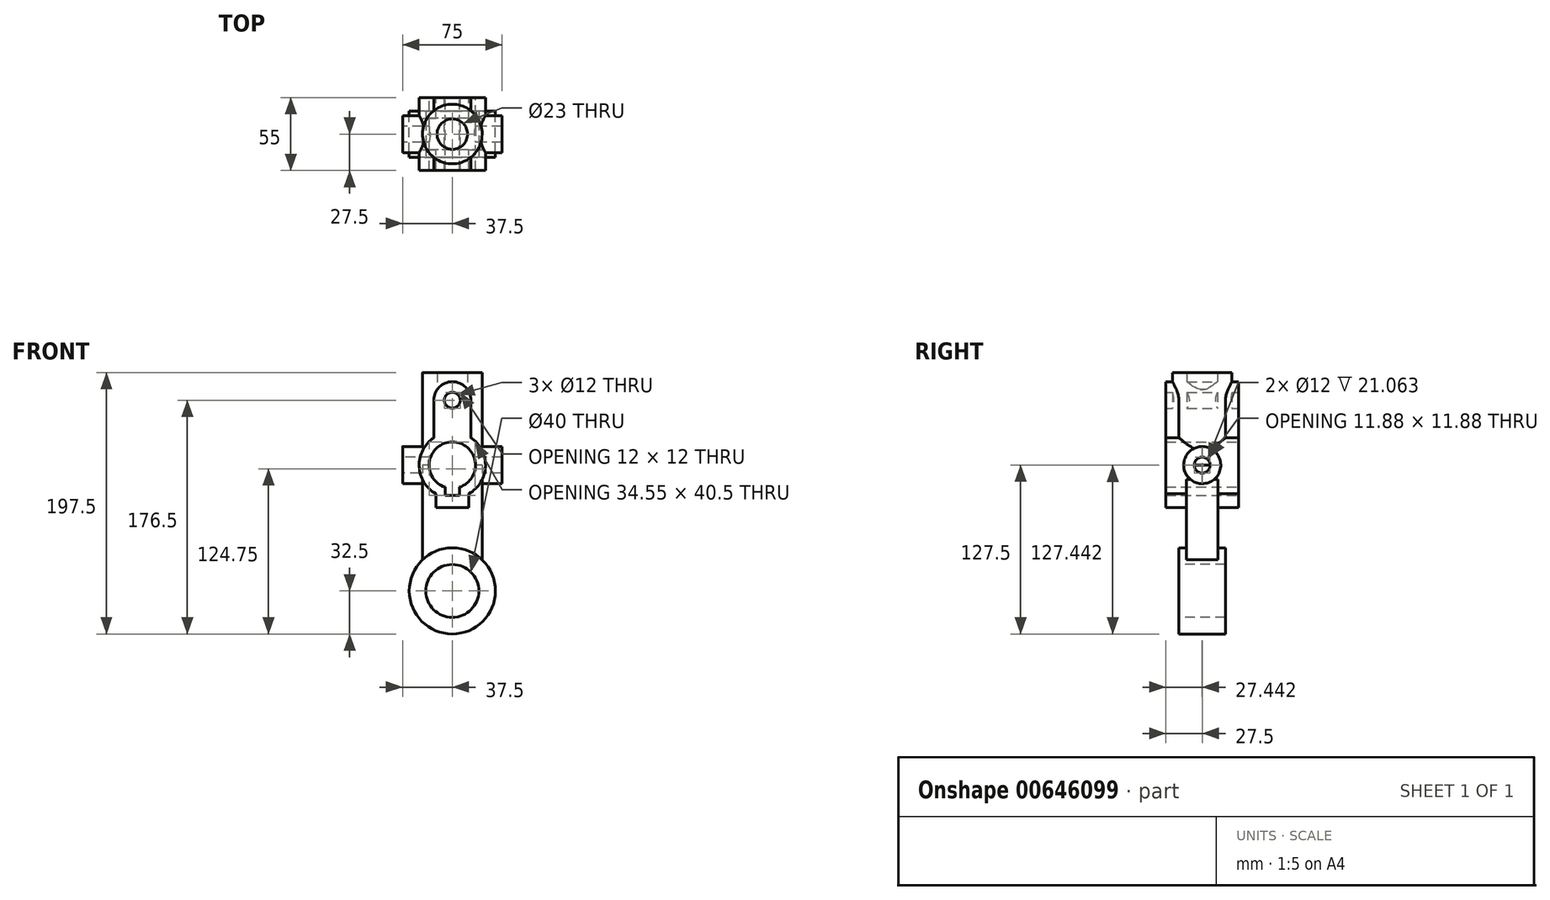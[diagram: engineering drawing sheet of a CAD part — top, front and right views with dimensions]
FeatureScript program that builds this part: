
annotation { "Feature Type Name" : "Feature", "Feature Type Description" : "" }
export const myFeature = defineFeature(function(context is Context, id is Id, definition is map)
    precondition{}
    {
        {
            var Q0;
            Q0=qCreatedBy(makeId("Top.planeOp"),FACE);
            var sketch = newSketch(context, id + "F0", { "sketchPlane" : qUnion([Q0])});
            skCircle(sketch, "E0", {"center": v(0, 0) * mm, "radius": 11.5 * mm});
            skCircle(sketch, "E1", {"center": v(0, 0) * mm, "radius": 22.5 * mm});
            skSolve(sketch);
        }
        {
            var Q0;
            Q0=makeQuery(id+"F0.imprint","IMPRINT",FACE,{"disambiguationData":[TD([[makeQuery(id+"F0.imprint","IMPRINT",EDGE,{"derivedFrom":sQuery(id+"F0.wireOp",EDGE,"E0")}),-1.0]])]});
            extrude(context, id + "F1", {"entities" : qUnion([Q0]), "depth" : 70 * mm, "offsetDistance" : 25 * mm});
        }
        {
            var Q0;
            Q0=qCreatedBy(makeId("Front.planeOp"),FACE);
            var sketch = newSketch(context, id + "F2", { "sketchPlane" : qUnion([Q0])});
            skArc(sketch, "E2", {"start": v(5.5, -16.61) * mm, "mid": v(0, 17.5) * mm, "end": v(-5.5, -16.61) * mm});
            skLineSegment(sketch, "E3", {"start": v(0, -23) * mm, "end": v(-5.5, -23) * mm});
            skLineSegment(sketch, "E4", {"start": v(-5.5, -23) * mm, "end": v(5.5, -23) * mm});
            skLineSegment(sketch, "E5", {"start": v(-5.5, -23) * mm, "end": v(-5.5, -16.61) * mm});
            skLineSegment(sketch, "E6", {"start": v(5.5, -23) * mm, "end": v(5.5, -16.61) * mm});
            skArc(sketch, "E7", {"start": v(12.5, -21.65) * mm, "mid": v(24.98, -0.88) * mm, "end": v(14, 20.71) * mm});
            skLineSegment(sketch, "E8", {"start": v(0, -32) * mm, "end": v(-12.5, -32) * mm});
            skLineSegment(sketch, "E9", {"start": v(0, -32) * mm, "end": v(12.5, -32) * mm});
            skLineSegment(sketch, "E10", {"start": v(12.5, -32) * mm, "end": v(12.5, -21.65) * mm});
            skLineSegment(sketch, "E11", {"start": v(-12.5, -32) * mm, "end": v(-12.5, -21.65) * mm});
            skPoint(sketch, "E12.endSnap0", {"position": v(0, 25) * mm});
            skCircle(sketch, "E13", {"center": v(0, 49) * mm, "radius": 6 * mm});
            skArc(sketch, "E14", {"start": v(14, 49) * mm, "mid": v(0, 63) * mm, "end": v(-14, 49) * mm});
            skLineSegment(sketch, "E15", {"start": v(-14, 49) * mm, "end": v(14, 49) * mm});
            skLineSegment(sketch, "E16", {"start": v(14, 49) * mm, "end": v(-14, 49) * mm});
            skLineSegment(sketch, "E17", {"start": v(-14, 49) * mm, "end": v(-14, 20.71) * mm});
            skLineSegment(sketch, "E18", {"start": v(14, 49) * mm, "end": v(14, 20.71) * mm});
            skPoint(sketch, "E12.end.orphan", {"position": v(0, 35) * mm});
            skPoint(sketch, "E12.start.orphan", {"position": v(0, 25) * mm});
            skArc(sketch, "E19.trimOffspring", {"start": v(-14, 20.71) * mm, "mid": v(-24.98, -0.88) * mm, "end": v(-12.5, -21.65) * mm});
            skSolve(sketch);
        }
        {
            var Q0;
            Q0 = qSketchRegion(id + "F2", true);
            extrude(context, id + "F3", {"entities" : qUnion([Q0]), "operationType" : NewBodyOperationType.ADD, "endBound" : BoundingType.SYMMETRIC, "depth" : 55 * mm, "offsetDistance" : 25 * mm});
        }
        {
            var Q0;
            Q0=qCreatedBy(makeId("Right.planeOp"),FACE);
            var sketch = newSketch(context, id + "F4", { "sketchPlane" : qUnion([Q0])});
            skCircle(sketch, "E20", {"center": v(0, 0) * mm, "radius": 14 * mm});
            skCircle(sketch, "E21", {"center": v(0, 0) * mm, "radius": 6 * mm});
            skSolve(sketch);
        }
        {
            var Q0;
            Q0 = qSketchRegion(id + "F4", true);
            extrude(context, id + "F5", {"entities" : qUnion([Q0]), "operationType" : NewBodyOperationType.ADD, "endBound" : BoundingType.SYMMETRIC, "depth" : 75 * mm, "offsetDistance" : 25 * mm});
        }
        {
            var Q0;
            Q0=makeQuery(id+"F5.opExtrude","CAP_FACE",FACE,{"disambiguationData":[OSD([sQuery(id+"F4.wireOp",EDGE,"E20"),sQuery(id+"F4.wireOp",EDGE,"E21")])],"isStart":true});
            var sketch = newSketch(context, id + "F6", { "sketchPlane" : qUnion([Q0])});
            skCircle(sketch, "E22", {"center": v(0, 0) * mm, "radius": 6 * mm});
            skSolve(sketch);
        }
        {
            var Q0;
            Q0 = qSketchRegion(id + "F6", true);
            extrude(context, id + "F7", {"entities" : qUnion([Q0]), "operationType" : NewBodyOperationType.REMOVE, "endBound" : BoundingType.THROUGH_ALL, "oppositeDirection" : true, "depth" : 25 * mm, "offsetDistance" : 25 * mm});
        }
        {
            var Q0;
            Q0=makeQuery(id+"F3.opExtrude","CAP_FACE",FACE,{"disambiguationData":[OSD([sQuery(id+"F2.wireOp",EDGE,"E2"),sQuery(id+"F2.wireOp",EDGE,"E4"),sQuery(id+"F2.wireOp",EDGE,"E5"),sQuery(id+"F2.wireOp",EDGE,"E6"),sQuery(id+"F2.wireOp",EDGE,"E7"),sQuery(id+"F2.wireOp",EDGE,"E8"),sQuery(id+"F2.wireOp",EDGE,"E9"),sQuery(id+"F2.wireOp",EDGE,"E10"),sQuery(id+"F2.wireOp",EDGE,"E11"),sQuery(id+"F2.wireOp",EDGE,"E13"),sQuery(id+"F2.wireOp",EDGE,"E14"),sQuery(id+"F2.wireOp",EDGE,"E17"),sQuery(id+"F2.wireOp",EDGE,"E18"),sQuery(id+"F2.wireOp",EDGE,"E19.trimOffspring")])],"isStart":false});
            var sketch = newSketch(context, id + "F8", { "sketchPlane" : qUnion([Q0])});
            skCircle(sketch, "E23", {"center": v(0, 0) * mm, "radius": 17.5 * mm});
            skSolve(sketch);
        }
        {
            var Q0;
            Q0 = qSketchRegion(id + "F8", true);
            extrude(context, id + "F9", {"entities" : qUnion([Q0]), "operationType" : NewBodyOperationType.REMOVE, "endBound" : BoundingType.THROUGH_ALL, "oppositeDirection" : true, "depth" : 25 * mm, "offsetDistance" : 25 * mm});
        }
        {
            var Q0;
            Q0=qCreatedBy(makeId("Top.planeOp"),FACE);
            var sketch = newSketch(context, id + "F10", { "sketchPlane" : qUnion([Q0])});
            skLineSegment(sketch, "E24", {"start": v(0, 0) * mm, "end": v(22.5, 0) * mm});
            skLineSegment(sketch, "E25", {"start": v(0, 0) * mm, "end": v(-22.5, 0) * mm});
            skLineSegment(sketch, "E26", {"start": v(0, 0) * mm, "end": v(0, -12) * mm});
            skLineSegment(sketch, "E27", {"start": v(0, 0) * mm, "end": v(0, 12) * mm});
            skLineSegment(sketch, "E28.bottom", {"start": v(-22.5, -12) * mm, "end": v(22.5, -12) * mm});
            skLineSegment(sketch, "E28.top", {"start": v(-22.5, 12) * mm, "end": v(22.5, 12) * mm});
            skLineSegment(sketch, "E28.left", {"start": v(-22.5, -12) * mm, "end": v(-22.5, 12) * mm});
            skLineSegment(sketch, "E28.right", {"start": v(22.5, -12) * mm, "end": v(22.5, 12) * mm});
            skSolve(sketch);
        }
        {
            var Q0;
            Q0 = qSketchRegion(id + "F10", true);
            extrude(context, id + "F11", {"entities" : qUnion([Q0]), "operationType" : NewBodyOperationType.ADD, "oppositeDirection" : true, "depth" : 95 * mm, "offsetDistance" : 25 * mm});
        }
        {
            var Q0;
            Q0=qCreatedBy(makeId("Front.planeOp"),FACE);
            var sketch = newSketch(context, id + "F12", { "sketchPlane" : qUnion([Q0])});
            skLineSegment(sketch, "E29", {"start": v(0, 0) * mm, "end": v(0, -95) * mm});
            skCircle(sketch, "E30", {"center": v(0, -95) * mm, "radius": 32.5 * mm});
            skSolve(sketch);
        }
        {
            var Q0;
            Q0 = qSketchRegion(id + "F12", true);
            extrude(context, id + "F13", {"entities" : qUnion([Q0]), "operationType" : NewBodyOperationType.ADD, "endBound" : BoundingType.SYMMETRIC, "depth" : 35 * mm, "offsetDistance" : 25 * mm});
        }
        {
            var Q0;
            Q0=makeQuery(id+"F13.opExtrude","CAP_FACE",FACE,{"disambiguationData":[OSD([sQuery(id+"F12.wireOp",EDGE,"E30")])],"isStart":false});
            var sketch = newSketch(context, id + "F14", { "sketchPlane" : qUnion([Q0])});
            skCircle(sketch, "E31", {"center": v(0, -95) * mm, "radius": 20 * mm});
            skSolve(sketch);
        }
        {
            var Q0;
            Q0 = qSketchRegion(id + "F14", true);
            extrude(context, id + "F15", {"entities" : qUnion([Q0]), "operationType" : NewBodyOperationType.REMOVE, "endBound" : BoundingType.THROUGH_ALL, "oppositeDirection" : true, "depth" : 25 * mm, "offsetDistance" : 25 * mm});
        }
        {
            var Q0;
            Q0=makeQuery(id+"F3.opExtrude","CAP_FACE",FACE,{"disambiguationData":[OSD([sQuery(id+"F2.wireOp",EDGE,"E2"),sQuery(id+"F2.wireOp",EDGE,"E4"),sQuery(id+"F2.wireOp",EDGE,"E5"),sQuery(id+"F2.wireOp",EDGE,"E6"),sQuery(id+"F2.wireOp",EDGE,"E7"),sQuery(id+"F2.wireOp",EDGE,"E8"),sQuery(id+"F2.wireOp",EDGE,"E9"),sQuery(id+"F2.wireOp",EDGE,"E10"),sQuery(id+"F2.wireOp",EDGE,"E11"),sQuery(id+"F2.wireOp",EDGE,"E13"),sQuery(id+"F2.wireOp",EDGE,"E14"),sQuery(id+"F2.wireOp",EDGE,"E17"),sQuery(id+"F2.wireOp",EDGE,"E18"),sQuery(id+"F2.wireOp",EDGE,"E19.trimOffspring")])],"isStart":false});
            var sketch = newSketch(context, id + "F16", { "sketchPlane" : qUnion([Q0])});
            skLineSegment(sketch, "E32", {"start": v(0, -23) * mm, "end": v(-5.5, -23) * mm});
            skLineSegment(sketch, "E33", {"start": v(0, -23) * mm, "end": v(5.5, -23) * mm});
            skLineSegment(sketch, "E34", {"start": v(5.5, -23) * mm, "end": v(5.5, -16.61) * mm});
            skLineSegment(sketch, "E35", {"start": v(-5.5, -23) * mm, "end": v(-5.5, -16.61) * mm});
            skPoint(sketch, "E36.center.orphan", {"position": v(0, 0) * mm});
            skLineSegment(sketch, "E37", {"start": v(5.5, -16.61) * mm, "end": v(-5.5, -16.61) * mm});
            skSolve(sketch);
        }
        {
            var Q0;
            Q0 = qSketchRegion(id + "F16", true);
            extrude(context, id + "F17", {"entities" : qUnion([Q0]), "operationType" : NewBodyOperationType.REMOVE, "endBound" : BoundingType.THROUGH_ALL, "oppositeDirection" : true, "depth" : 25 * mm, "offsetDistance" : 25 * mm});
        }
        {
            var Q0;
            Q0=makeQuery(id+"F3.opExtrude","CAP_FACE",FACE,{"disambiguationData":[OSD([sQuery(id+"F2.wireOp",EDGE,"E2"),sQuery(id+"F2.wireOp",EDGE,"E4"),sQuery(id+"F2.wireOp",EDGE,"E5"),sQuery(id+"F2.wireOp",EDGE,"E6"),sQuery(id+"F2.wireOp",EDGE,"E7"),sQuery(id+"F2.wireOp",EDGE,"E8"),sQuery(id+"F2.wireOp",EDGE,"E9"),sQuery(id+"F2.wireOp",EDGE,"E10"),sQuery(id+"F2.wireOp",EDGE,"E11"),sQuery(id+"F2.wireOp",EDGE,"E13"),sQuery(id+"F2.wireOp",EDGE,"E14"),sQuery(id+"F2.wireOp",EDGE,"E17"),sQuery(id+"F2.wireOp",EDGE,"E18"),sQuery(id+"F2.wireOp",EDGE,"E19.trimOffspring")])],"isStart":false});
            var sketch = newSketch(context, id + "F18", { "sketchPlane" : qUnion([Q0])});
            skCircle(sketch, "E38", {"center": v(0, 0) * mm, "radius": 17.5 * mm});
            skSolve(sketch);
        }
        {
            var Q0;
            Q0 = qSketchRegion(id + "F18", true);
            extrude(context, id + "F19", {"entities" : qUnion([Q0]), "operationType" : NewBodyOperationType.REMOVE, "endBound" : BoundingType.THROUGH_ALL, "oppositeDirection" : true, "depth" : 25 * mm, "offsetDistance" : 25 * mm});
        }
    });
